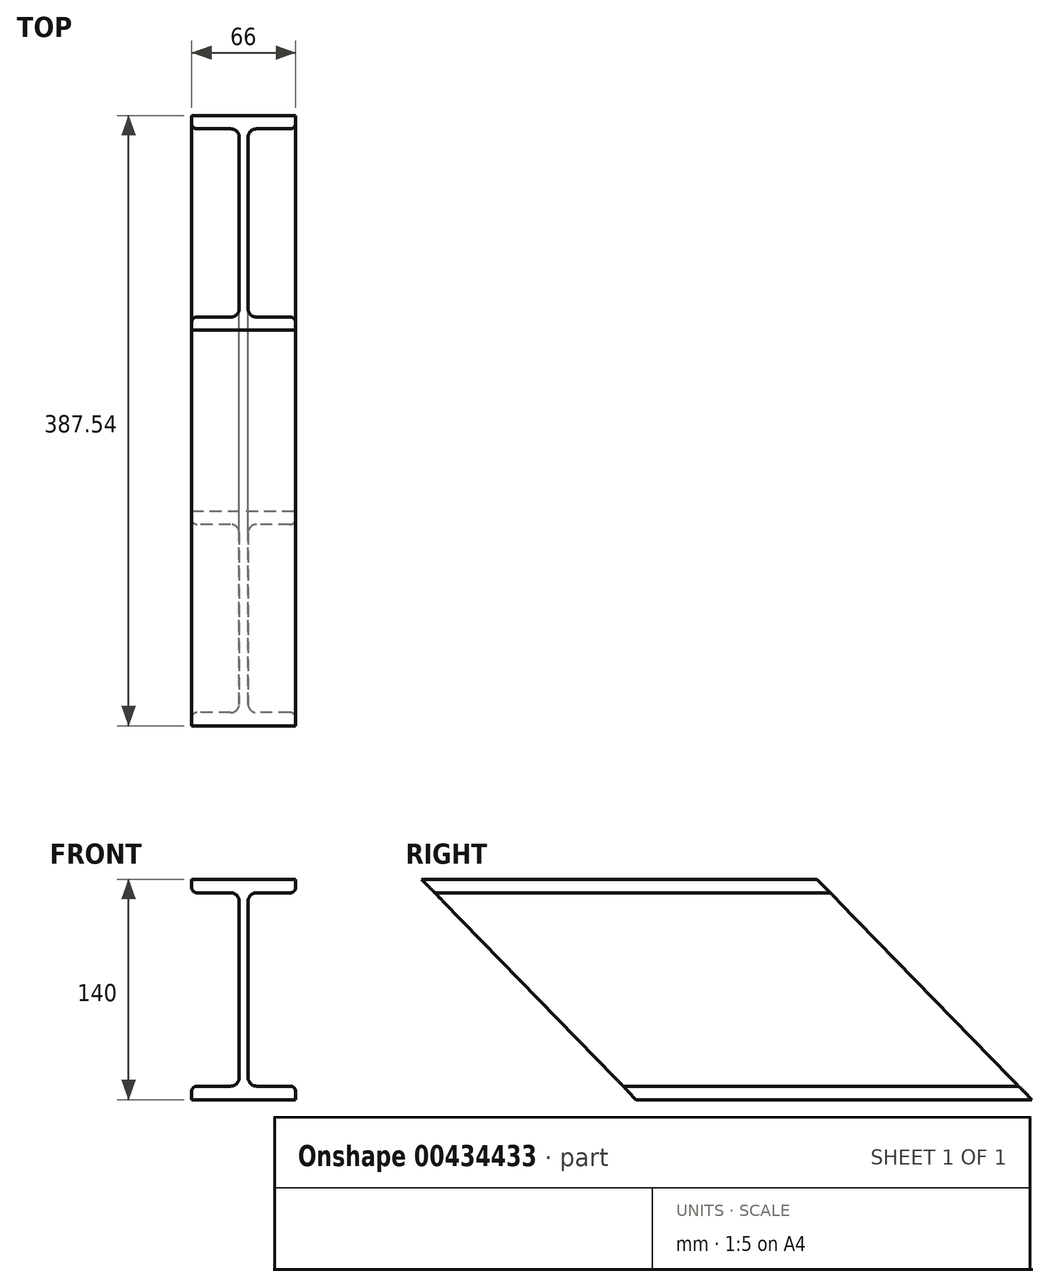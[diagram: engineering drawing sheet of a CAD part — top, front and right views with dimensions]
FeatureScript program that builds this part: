
annotation { "Feature Type Name" : "Feature", "Feature Type Description" : "" }
export const myFeature = defineFeature(function(context is Context, id is Id, definition is map)
    precondition{}
    {
        {
            var Q0;
            Q0=qCreatedBy(makeId("Front.planeOp"),FACE);
            var sketch = newSketch(context, id + "F0", { "sketchPlane" : qUnion([Q0])});
            skLineSegment(sketch, "E0.bottom", {"start": v(-33, 70) * mm, "end": v(33, 70) * mm});
            skLineSegment(sketch, "E0.top", {"start": v(-33, 61.4) * mm, "end": v(-2.85, 61.4) * mm});
            skLineSegment(sketch, "E0.left", {"start": v(-33, 70) * mm, "end": v(-33, 61.4) * mm});
            skLineSegment(sketch, "E0.right", {"start": v(33, 70) * mm, "end": v(33, 61.4) * mm});
            skLineSegment(sketch, "E1.bottom", {"start": v(-33, -61.4) * mm, "end": v(-2.85, -61.4) * mm});
            skLineSegment(sketch, "E1.top", {"start": v(-33, -70) * mm, "end": v(33, -70) * mm});
            skLineSegment(sketch, "E1.left", {"start": v(-33, -61.4) * mm, "end": v(-33, -70) * mm});
            skLineSegment(sketch, "E1.right", {"start": v(33, -61.4) * mm, "end": v(33, -70) * mm});
            skLineSegment(sketch, "E2.left", {"start": v(-2.85, 61.4) * mm, "end": v(-2.85, -61.4) * mm});
            skLineSegment(sketch, "E2.right", {"start": v(2.85, 61.4) * mm, "end": v(2.85, -61.4) * mm});
            skPoint(sketch, "E3.endSnap0", {"position": v(0, -61.4) * mm});
            skLineSegment(sketch, "E4.trimOffspring", {"start": v(2.85, 61.4) * mm, "end": v(33, 61.4) * mm});
            skLineSegment(sketch, "E5.trimOffspring", {"start": v(2.85, -61.4) * mm, "end": v(33, -61.4) * mm});
            skLineSegment(sketch, "E6", {"start": v(0, 70) * mm, "end": v(0, -70) * mm, "construction": true});
            skSolve(sketch);
        }
        {
            var Q0;
            Q0=qSketchRegion(id+"F0",true);
            extrude(context, id + "F1", {"entities" : qUnion([Q0]), "endBound" : BoundingType.SYMMETRIC, "depth" : 4500 * mm});
        }
        {
            var Q0;
            Q0=qCreatedBy(makeId("Right.planeOp"),FACE);
            var sketch = newSketch(context, id + "F2", { "sketchPlane" : qUnion([Q0])});
            skLineSegment(sketch, "E7", {"start": v(-1254.9, 70) * mm, "end": v(450.72, -1681.82) * mm});
            skLineSegment(sketch, "E8", {"start": v(450.72, -1681.82) * mm, "end": v(2250, 70) * mm});
            skLineSegment(sketch, "E9.top", {"start": v(-2250, -1681.82) * mm, "end": v(2250, -1681.82) * mm});
            skLineSegment(sketch, "E9.right", {"start": v(2250, 70) * mm, "end": v(2250, -1681.82) * mm});
            skLineSegment(sketch, "E10", {"start": v(-1254.9, 70) * mm, "end": v(-2250, 70) * mm});
            skLineSegment(sketch, "E11", {"start": v(-2250, 70) * mm, "end": v(-2250, -1681.82) * mm});
            skSolve(sketch);
        }
        {
            var Q0;
            Q0=makeQuery(id+"F1.opExtrude","SWEPT_EDGE",EDGE,{"disambiguationData":[OSD([sQuery(id+"F0.wireOp",EDGE,"E2.right"),sQuery(id+"F0.wireOp",EDGE,"E4.trimOffspring")])]});
            var Q1;
            Q1=makeQuery(id+"F1.opExtrude","SWEPT_EDGE",EDGE,{"disambiguationData":[OSD([sQuery(id+"F0.wireOp",EDGE,"E0.top"),sQuery(id+"F0.wireOp",EDGE,"E2.left")])]});
            var Q2;
            Q2=makeQuery(id+"F1.opExtrude","SWEPT_EDGE",EDGE,{"disambiguationData":[OSD([sQuery(id+"F0.wireOp",EDGE,"E1.bottom"),sQuery(id+"F0.wireOp",EDGE,"E2.left")])]});
            var Q3;
            Q3=makeQuery(id+"F1.opExtrude","SWEPT_EDGE",EDGE,{"disambiguationData":[OSD([sQuery(id+"F0.wireOp",EDGE,"E2.right"),sQuery(id+"F0.wireOp",EDGE,"E5.trimOffspring")])]});
            fillet(context, id + "F3", {"entities" : qUnion([Q0, Q1, Q2, Q3]), "radius" : 5.4 * mm, "tangentPropagation" : true, "allowEdgeOverflow" : false});
        }
        {
            var Q0;
            Q0=qSketchRegion(id+"F2",true);
            extrude(context, id + "F4", {"entities" : qUnion([Q0]), "operationType" : NewBodyOperationType.REMOVE, "endBound" : BoundingType.THROUGH_ALL, "oppositeDirection" : true, "depth" : 25 * mm, "hasSecondDirection" : true, "secondDirectionBound" : SecondDirectionBoundingType.THROUGH_ALL, "secondDirectionOppositeDirection" : false, "secondDirectionDepth" : 25 * mm});
        }
        {
            var Q0;
            Q0=qCreatedBy(makeId("Right.planeOp"),FACE);
            var sketch = newSketch(context, id + "F5", { "sketchPlane" : qUnion([Q0])});
            skLineSegment(sketch, "E12", {"start": v(1602.61, 70) * mm, "end": v(-1254.9, 70) * mm});
            skLineSegment(sketch, "E13", {"start": v(-1254.9, 70) * mm, "end": v(-1118.6, -70) * mm});
            skLineSegment(sketch, "E14", {"start": v(-1118.6, -70) * mm, "end": v(1738.92, -70) * mm});
            skLineSegment(sketch, "E15", {"start": v(1738.92, -70) * mm, "end": v(1602.61, 70) * mm});
            skLineSegment(sketch, "E16", {"start": v(2213.45, 232.6) * mm, "end": v(1656.51, -309.65) * mm, "construction": true});
            skPoint(sketch, "E17", {"position": v(2046.44, 70) * mm});
            skLineSegment(sketch, "E18", {"start": v(1990.15, -70) * mm, "end": v(1853.84, 70) * mm});
            skLineSegment(sketch, "E19", {"start": v(1853.84, 70) * mm, "end": v(2250, 70) * mm});
            skLineSegment(sketch, "E20", {"start": v(2250, 70) * mm, "end": v(2106.2, -70) * mm});
            skLineSegment(sketch, "E21", {"start": v(2106.2, -70) * mm, "end": v(1990.15, -70) * mm});
            skSolve(sketch);
        }
        {
            var Q0;
            Q0 = qSketchRegion(id + "F5", true);
            extrude(context, id + "F6", {"entities" : qUnion([Q0]), "operationType" : NewBodyOperationType.REMOVE, "endBound" : BoundingType.THROUGH_ALL, "oppositeDirection" : true, "depth" : 25 * mm, "hasSecondDirection" : true, "secondDirectionBound" : SecondDirectionBoundingType.THROUGH_ALL, "secondDirectionOppositeDirection" : false, "secondDirectionDepth" : 25 * mm});
        }
        {
            var Q0;
            Q0=makeQuery(id+"F1.opExtrude","SWEPT_EDGE",EDGE,{"disambiguationData":[OSD([sQuery(id+"F0.wireOp",EDGE,"E1.bottom"),sQuery(id+"F0.wireOp",EDGE,"E1.left")])]});
            var Q1;
            Q1=makeQuery(id+"F1.opExtrude","SWEPT_EDGE",EDGE,{"disambiguationData":[OSD([sQuery(id+"F0.wireOp",EDGE,"E0.top"),sQuery(id+"F0.wireOp",EDGE,"E0.left")])]});
            var Q2;
            Q2=makeQuery(id+"F1.opExtrude","SWEPT_EDGE",EDGE,{"disambiguationData":[OSD([sQuery(id+"F0.wireOp",EDGE,"E1.right"),sQuery(id+"F0.wireOp",EDGE,"E5.trimOffspring")])]});
            var Q3;
            Q3=makeQuery(id+"F1.opExtrude","SWEPT_EDGE",EDGE,{"disambiguationData":[OSD([sQuery(id+"F0.wireOp",EDGE,"E0.right"),sQuery(id+"F0.wireOp",EDGE,"E4.trimOffspring")])]});
            fillet(context, id + "F7", {"entities" : qUnion([Q0, Q1, Q2, Q3]), "radius" : 3.4 * mm, "tangentPropagation" : true, "allowEdgeOverflow" : false});
        }
    });
